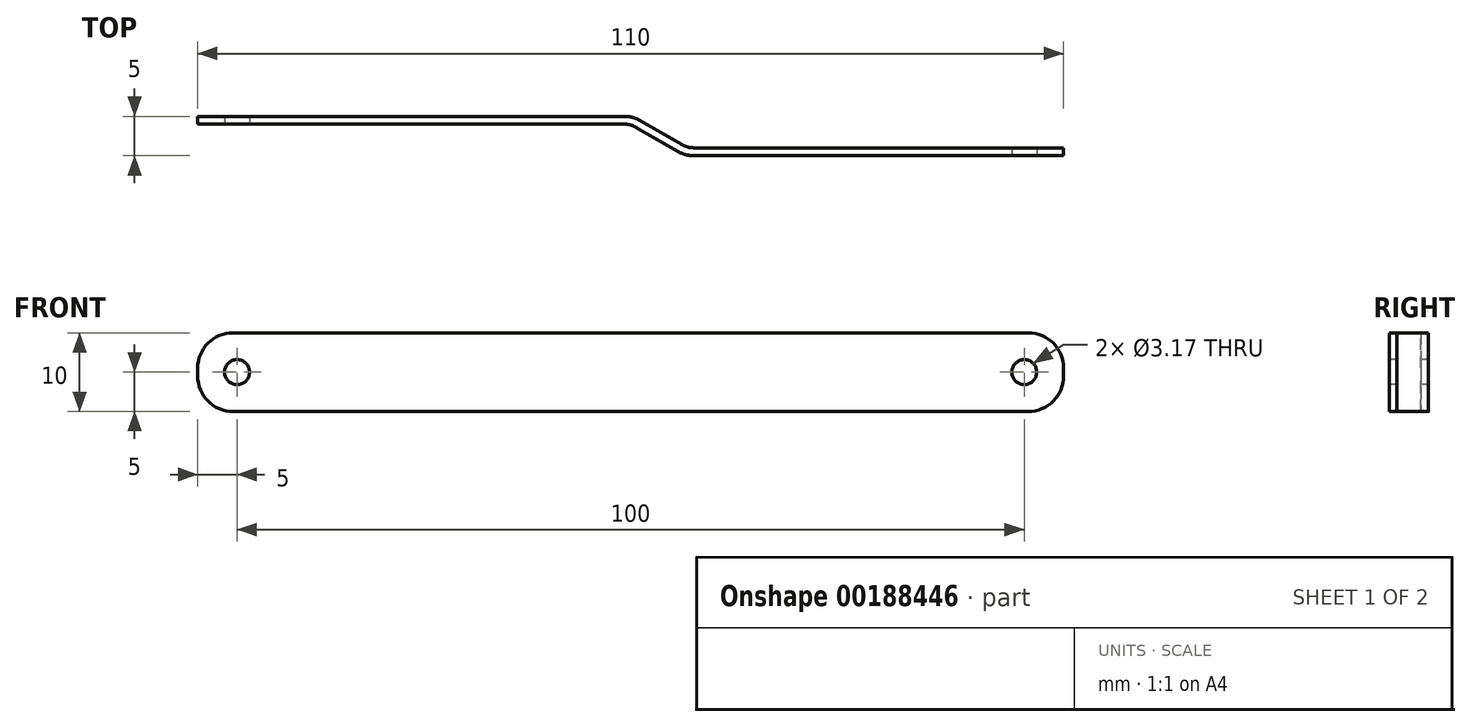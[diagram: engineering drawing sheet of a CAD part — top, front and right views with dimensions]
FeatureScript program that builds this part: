
annotation { "Feature Type Name" : "Feature", "Feature Type Description" : "" }
export const myFeature = defineFeature(function(context is Context, id is Id, definition is map)
    precondition{}
    {
        {
            var Q0;
            Q0=qCreatedBy(makeId("Top.planeOp"),FACE);
            var sketch = newSketch(context, id + "F0", { "sketchPlane" : qUnion([Q0])});
            skLineSegment(sketch, "E0", {"start": v(-69.02, 0) * mm, "end": v(67.73, 0) * mm, "construction": true});
            skLineSegment(sketch, "E1", {"start": v(-5, 15) * mm, "end": v(49.2, 15) * mm});
            skLineSegment(sketch, "E2", {"start": v(50.7, 14.6) * mm, "end": v(56, 11.54) * mm});
            skLineSegment(sketch, "E3", {"start": v(58, 11) * mm, "end": v(105, 11) * mm});
            skLineSegment(sketch, "E4.0", {"start": v(58, 12) * mm, "end": v(105, 12) * mm});
            skLineSegment(sketch, "E4.1", {"start": v(51.2, 15.46) * mm, "end": v(56.5, 12.4) * mm});
            skLineSegment(sketch, "E4.2", {"start": v(-5, 16) * mm, "end": v(49.2, 16) * mm});
            skLineSegment(sketch, "E5", {"start": v(-5, 15) * mm, "end": v(-5, 16) * mm});
            skLineSegment(sketch, "E6", {"start": v(105, 11) * mm, "end": v(105, 12) * mm});
            skLineSegment(sketch, "E7", {"start": v(0, 21.54) * mm, "end": v(0, 11.72) * mm, "construction": true});
            skLineSegment(sketch, "E8", {"start": v(100, 14.11) * mm, "end": v(100, 8.75) * mm, "construction": true});
            skPoint(sketch, "E9.visualSharp", {"position": v(50, 15) * mm});
            skArc(sketch, "E9.filletArc", {"start": v(50.7, 14.6) * mm, "mid": v(49.97, 14.9) * mm, "end": v(49.2, 15) * mm});
            skPoint(sketch, "E10.visualSharp", {"position": v(50.27, 16) * mm});
            skArc(sketch, "E10.filletArc", {"start": v(51.2, 15.46) * mm, "mid": v(50.23, 15.86) * mm, "end": v(49.2, 16) * mm});
            skPoint(sketch, "E11.visualSharp", {"position": v(57.2, 12) * mm});
            skArc(sketch, "E11.filletArc", {"start": v(56.5, 12.4) * mm, "mid": v(57.22, 12.1) * mm, "end": v(58, 12) * mm});
            skPoint(sketch, "E12.visualSharp", {"position": v(56.93, 11) * mm});
            skArc(sketch, "E12.filletArc", {"start": v(56, 11.54) * mm, "mid": v(56.96, 11.14) * mm, "end": v(58, 11) * mm});
            skSolve(sketch);
        }
        {
            var Q0;
            Q0 = qSketchRegion(id + "F0", true);
            extrude(context, id + "F1", {"entities" : qUnion([Q0]), "endBound" : BoundingType.SYMMETRIC, "depth" : 10 * mm, "offsetDistance" : 25 * mm});
        }
        {
            var Q0;
            Q0=qCreatedBy(makeId("Front.planeOp"),FACE);
            var sketch = newSketch(context, id + "F2", { "sketchPlane" : qUnion([Q0])});
            skPoint(sketch, "E13", {"position": v(0, 0) * mm});
            skPoint(sketch, "E14", {"position": v(100, 0) * mm});
            skSolve(sketch);
        }
        {
            var Q0;
            Q0=sQuery(id+"F2.wireOp",VERTEX,"E13");
            var Q1;
            Q1=sQuery(id+"F2.wireOp",VERTEX,"E14");
            var Q2;
            Q2=makeQuery(id+"F1.opExtrude","SWEPT_BODY",BODY,{"disambiguationData":[OSD([sQuery(id+"F0.wireOp",EDGE,"E1"),sQuery(id+"F0.wireOp",EDGE,"E2"),sQuery(id+"F0.wireOp",EDGE,"E3"),sQuery(id+"F0.wireOp",EDGE,"E4.0"),sQuery(id+"F0.wireOp",EDGE,"E4.1"),sQuery(id+"F0.wireOp",EDGE,"E4.2"),sQuery(id+"F0.wireOp",EDGE,"E5"),sQuery(id+"F0.wireOp",EDGE,"E6"),sQuery(id+"F0.wireOp",EDGE,"E9.filletArc"),sQuery(id+"F0.wireOp",EDGE,"E10.filletArc"),sQuery(id+"F0.wireOp",EDGE,"E11.filletArc"),sQuery(id+"F0.wireOp",EDGE,"E12.filletArc")])]});
            hole(context, id + "F3", {"style" : HoleStyle.SIMPLE, "endStyle" : HoleEndStyle.THROUGH, "holeDiameter" : 3.17 * mm, "majorDiameter" : 5 * mm, "isTappedThrough" : true, "tappedDepth" : 12 * mm, "tapClearance" : 3, "startFromSketch" : true, "locations" : qUnion([Q0, Q1]), "scope" : qUnion([Q2])});
        }
        {
            var Q0;
            Q0=makeQuery(id+"F1.opExtrude","CAP_EDGE",EDGE,{"disambiguationData":[OSD([sQuery(id+"F0.wireOp",EDGE,"E6")])],"isStart":false});
            var Q1;
            Q1=makeQuery(id+"F1.opExtrude","CAP_EDGE",EDGE,{"disambiguationData":[OSD([sQuery(id+"F0.wireOp",EDGE,"E6")])],"isStart":true});
            var Q2;
            Q2=makeQuery(id+"F1.opExtrude","CAP_EDGE",EDGE,{"disambiguationData":[OSD([sQuery(id+"F0.wireOp",EDGE,"E5")])],"isStart":false});
            var Q3;
            Q3=makeQuery(id+"F1.opExtrude","CAP_EDGE",EDGE,{"disambiguationData":[OSD([sQuery(id+"F0.wireOp",EDGE,"E5")])],"isStart":true});
            fillet(context, id + "F4", {"entities" : qUnion([Q0, Q1, Q2, Q3]), "radius" : 4.5 * mm, "tangentPropagation" : true, "allowEdgeOverflow" : false});
        }
    });
